# Revit family: AFX-Gilbert-Outdoor_Sconce
name_source: partatom
category: Lighting Fixtures
units: mm (PartAtom-declared; Revit-internal decimal feet)

## family parameters
Cut with Voids When Loaded = No
Host = Face
Light Source = Yes
Part Type = Normal
Room Calculation Point = No
Round Connector Dimension = Use Diameter
Shared = No

## types (2) — shared parameters
Apparent Load = 0 VA
Arm Finish = AFX - Black Steel
Assembly Code = D5020200
Color Filter = 16777215
Default Elevation = 48"
Diffuser Finish = AFX - White Acrylic
Dimming Lamp Color Temperature Shift = <None>
Emit from Line Length = 4"
Housing Finish = AFX - Black Steel
Keynote = 12500
Manufacturer = AFX Inc
Power Factor = 1
Product Documentation Link = https://www.afxinc.com
Revit File Built By = https://servex-us.com
Screem Finish = AFX - Black Steel
Tilt Angle = 90.00°
Type Comments = Gilbert
URL = https://www.afxinc.com
Voltage = 120 V
Wattage Comments = 9

## per-type parameters (varying)
| type | Arm1 | Arm2 | Colour Rendering Index | Depth | Description | Diffuser 1 | Disffuser 2 | Dist Screen | Height | Housing 1 | Housing 2 | Photometric Web File | Width |
| GILW0707LAJENBK | No | Yes | 80 | 12 1/4" | Outdoor LED Wall light Meta Housing And Polycarbonate Diffuser - 7 1/2"W x 12 1/4"D x 7 1/2"H | No | Yes | 7 41/64" | 7 1/2" | No | Yes | DTD310 35W 3000K_IESNA2002.IES | 7 1/2" |
| GILW1210LAJENBK | Yes | No | 90 | 17 1/4" | Outdoor LED wall light Meta Housing And Polycarbonate Diffuser - 11 1/2"W x 17 1/4"D x 10 1/4"H | Yes | No | 10 35/64" | 11 1/4" | Yes | No | DTD330 80W 3000K_IESNA2002.IES | 11 1/2" |

note: column(s) folded — value = type name in every type: Model

## geometry (parser evidence)
native form markers: Sweep x7
no freeform markers — native parametric forms only
